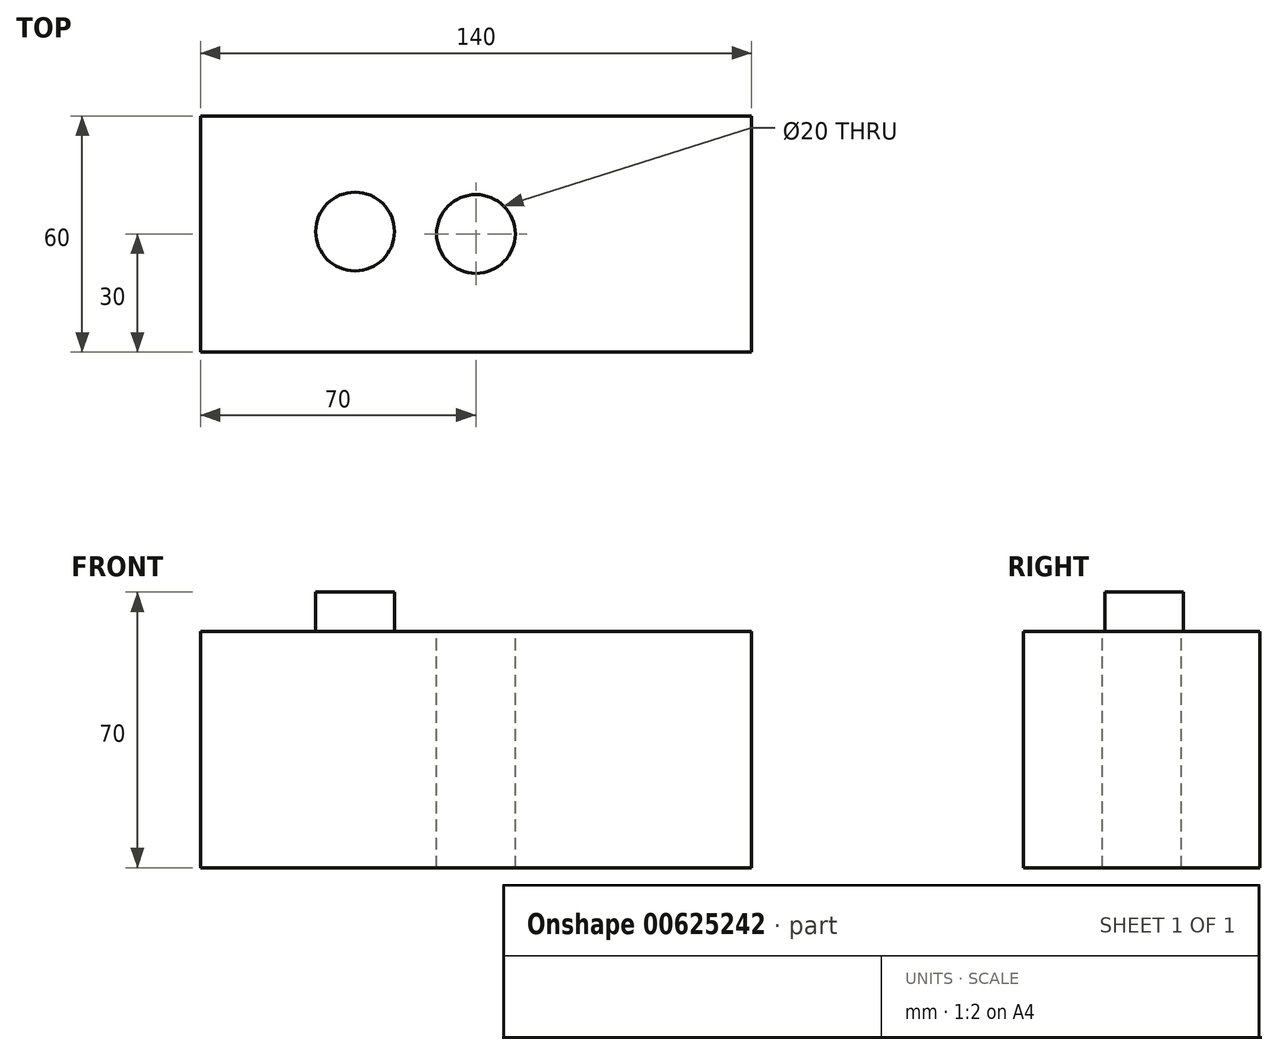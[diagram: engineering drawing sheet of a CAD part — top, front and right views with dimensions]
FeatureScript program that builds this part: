
annotation { "Feature Type Name" : "Feature", "Feature Type Description" : "" }
export const myFeature = defineFeature(function(context is Context, id is Id, definition is map)
    precondition{}
    {
        {
            var Q0;
            Q0=qCreatedBy(makeId("Top.planeOp"),FACE);
            var sketch = newSketch(context, id + "F0", { "sketchPlane" : qUnion([Q0])});
            skLineSegment(sketch, "E0.bottom", {"start": v(70, -30) * mm, "end": v(-70, -30) * mm});
            skLineSegment(sketch, "E0.top", {"start": v(70, 30) * mm, "end": v(-70, 30) * mm});
            skLineSegment(sketch, "E0.left", {"start": v(70, -30) * mm, "end": v(70, 30) * mm});
            skLineSegment(sketch, "E0.right", {"start": v(-70, -30) * mm, "end": v(-70, 30) * mm});
            skPoint(sketch, "E0.middle", {"position": v(0, 0) * mm});
            skSolve(sketch);
        }
        {
            var Q0;
            Q0 = qSketchRegion(id + "F0", true);
            extrude(context, id + "F1", {"entities" : qUnion([Q0]), "depth" : 60 * mm, "offsetDistance" : 25 * mm});
        }
        {
            var Q0;
            Q0=makeQuery(id+"F1.opExtrude","CAP_FACE",FACE,{"disambiguationData":[OSD([sQuery(id+"F0.wireOp",EDGE,"E0.bottom"),sQuery(id+"F0.wireOp",EDGE,"E0.top"),sQuery(id+"F0.wireOp",EDGE,"E0.left"),sQuery(id+"F0.wireOp",EDGE,"E0.right")])],"isStart":false});
            var sketch = newSketch(context, id + "F2", { "sketchPlane" : qUnion([Q0])});
            skLineSegment(sketch, "E1", {"start": v(-70, 0) * mm, "end": v(-50, 0) * mm});
            skLineSegment(sketch, "E2", {"start": v(70, 0) * mm, "end": v(50, 0) * mm});
            skPoint(sketch, "E2.endSnap0", {"position": v(70, 0) * mm});
            skSolve(sketch);
        }
        {
            var Q0;
            {var subQ3=makeQuery(id+"F1.opExtrude","CAP_EDGE",EDGE,{"disambiguationData":[OSD([sQuery(id+"F0.wireOp",EDGE,"E0.bottom")])],"isStart":false});Q0=makeQuery(id+"F2.imprint","IMPRINT",FACE,{"disambiguationData":[TD([[makeQuery(id+"F2.imprint","IMPRINT",EDGE,{"derivedFrom":subQ3}),-1.0]])]});}
            var sketch = newSketch(context, id + "F3", { "sketchPlane" : qUnion([Q0])});
            skCircle(sketch, "E3", {"center": v(-30.7, 0.62) * mm, "radius": 10 * mm});
            skPoint(sketch, "E3.first.point", {"position": v(-40.68, 0) * mm});
            skPoint(sketch, "E3.second.point", {"position": v(-20.72, 0) * mm});
            skPoint(sketch, "E3.third.point", {"position": v(-35.9, -7.92) * mm});
            skSolve(sketch);
        }
        {
            var Q0;
            {var subQ3=makeQuery(id+"F1.opExtrude","CAP_EDGE",EDGE,{"disambiguationData":[OSD([sQuery(id+"F0.wireOp",EDGE,"E0.bottom")])],"isStart":false});Q0=makeQuery(id+"F2.imprint","IMPRINT",FACE,{"disambiguationData":[TD([[makeQuery(id+"F2.imprint","IMPRINT",EDGE,{"derivedFrom":subQ3}),-1.0]])]});}
            var sketch = newSketch(context, id + "F4", { "sketchPlane" : qUnion([Q0])});
            skCircle(sketch, "E4", {"center": v(0, 0) * mm, "radius": 10 * mm});
            skSolve(sketch);
        }
        {
            var Q0;
            Q0 = qSketchRegion(id + "F3", true);
            extrude(context, id + "F5", {"entities" : qUnion([Q0]), "operationType" : NewBodyOperationType.ADD, "depth" : 10 * mm, "offsetDistance" : 25 * mm});
        }
        {
            var Q0;
            Q0 = qSketchRegion(id + "F4", true);
            extrude(context, id + "F6", {"entities" : qUnion([Q0]), "operationType" : NewBodyOperationType.REMOVE, "oppositeDirection" : true, "depth" : 73.6 * mm, "offsetDistance" : 25 * mm});
        }
    });
